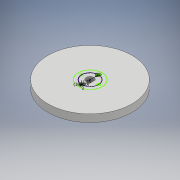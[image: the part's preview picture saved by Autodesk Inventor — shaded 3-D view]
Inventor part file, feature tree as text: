
AUTODESK INVENTOR PART (.ipt)
format: ipt  version: 2017 (Build 210142000, 142)  size: 181,760 bytes
history: native  units: mm
features: sketch x7, extrude x5, revolve x1
ambient origin geometry x8: Origin, YZ Plane, XZ Plane, XY Plane, X Axis, Y Axis, Z Axis, Center Point
bodies: Solid1 (feature_tree)
feature tree (13):
  revolve  "Revolution1"  Angle=90.0deg
  sketch  "Sketch3"  dims[d2=8.0mm d3=90.0deg]
  extrude  "Extrusion1"  TaperAngle=90.0deg  [1 undecoded]
  extrude  "Extrusion2"  TaperAngle=90.0deg  [1 undecoded]
  sketch  "Sketch5"  dims[d6=2.5mm d7=90.0deg]
  extrude  "Extrusion3"  TaperAngle=90.0deg  [1 undecoded]
  extrude  "Extrusion4"  TaperAngle=0.0deg  [1 undecoded]
  extrude  "Extrusion5"  Depth=5.0mm
  sketch  "Sketch1"  dims[d0=30.0mm d1=90.0deg]
  sketch  "Sketch4"  dims[d4=7.0mm d5=90.0deg]
  sketch  "Sketch6"  dims[d8=2.5mm d9=0.0mm]
  sketch  "Sketch7"  dims[d10=5.0mm d11=20.0mm]
  sketch  "Sketch8"  dims[d12=90.0deg d13=90.0deg d14=24.0mm d15=3.0mm d16=8.0mm d17=3.0mm d18=5.0mm d19=24.0mm d20=0.0mm d21=24.0mm d22=0.0mm d23=11.25mm d24=2.0mm d25=40.0mm d27=360.0deg d29=11.0mm d30=3.0mm d31=20.0mm d33=360.0deg d35=13.0mm d36=0.0mm d37=11.0mm d38=3.0mm d39=20.0mm d41=360.0deg d43=13.0mm d44=0.0mm d45=5.75mm d46=1.0mm d47=100.0mm d48=0.0mm]
note: 4 required parameter values undecoded (feature->parameter linkage not recoverable at this tier; creation-order binding heuristic only, values carry confidence <= 0.55)
